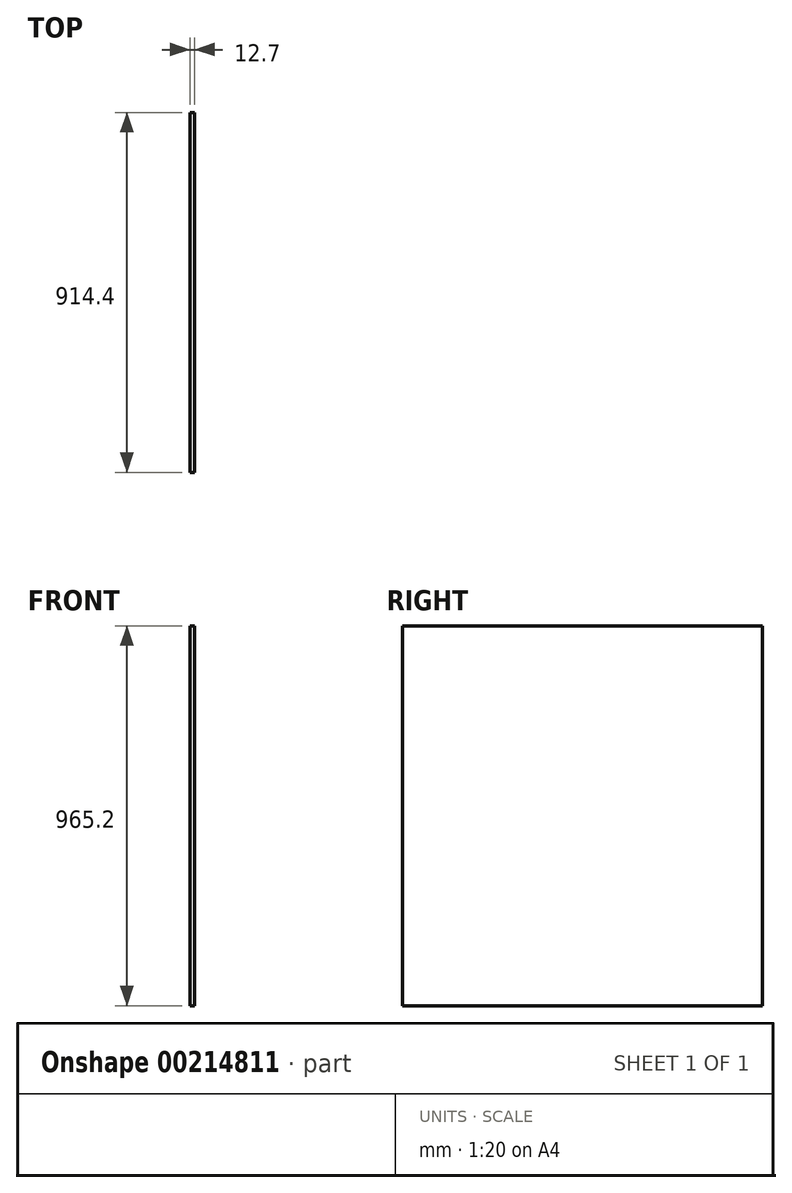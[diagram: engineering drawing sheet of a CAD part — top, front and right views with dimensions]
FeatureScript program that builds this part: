
annotation { "Feature Type Name" : "Feature", "Feature Type Description" : "" }
export const myFeature = defineFeature(function(context is Context, id is Id, definition is map)
    precondition{}
    {
        {
            var Q0;
            Q0=qCreatedBy(makeId("Right.planeOp"),FACE);
            var sketch = newSketch(context, id + "F0", { "sketchPlane" : qUnion([Q0])});
            skLineSegment(sketch, "E0.bottom", {"start": v(0, 0) * mm, "end": v(914.4, 0) * mm});
            skLineSegment(sketch, "E0.top", {"start": v(0, -965.2) * mm, "end": v(914.4, -965.2) * mm});
            skLineSegment(sketch, "E0.left", {"start": v(0, 0) * mm, "end": v(0, -965.2) * mm});
            skLineSegment(sketch, "E0.right", {"start": v(914.4, 0) * mm, "end": v(914.4, -965.2) * mm});
            skSolve(sketch);
        }
        {
            var Q0;
            Q0=makeQuery(id+"F0.imprint","IMPRINT",FACE,{"disambiguationData":[TD([[makeQuery(id+"F0.imprint","IMPRINT",EDGE,{"derivedFrom":sQuery(id+"F0.wireOp",EDGE,"E0.bottom")}),-1.0]])]});
            extrude(context, id + "F1", {"entities" : qUnion([Q0]), "depth" : 12.7 * mm});
        }
    });
